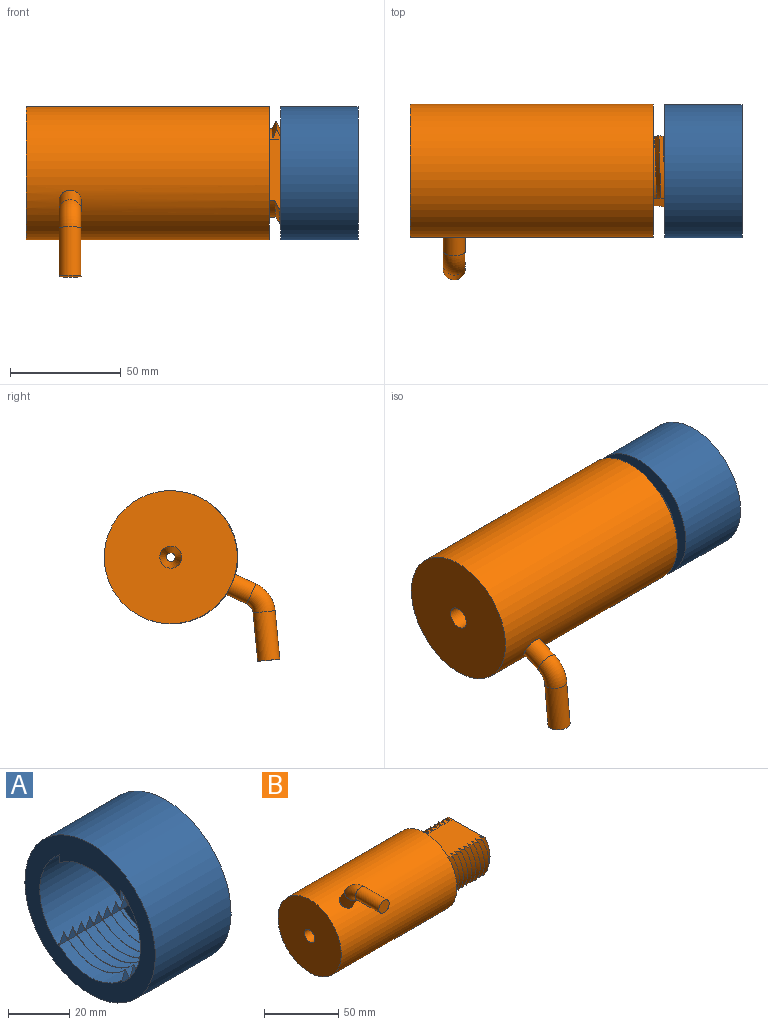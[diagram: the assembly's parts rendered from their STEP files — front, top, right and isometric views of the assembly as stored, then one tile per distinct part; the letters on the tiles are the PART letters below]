
ASSEMBLY  parts=2 mates=1
PART A: 97 faces, bbox 35x60.2x60.2 mm
  f0: cylinder r=20.1mm len=15.47mm, axis (-1,0,0), area 1.6mm2, adj f16,f25
  f1: cylinder r=20.1mm len=28.28mm, axis (-1,0,0), area 3.3mm2, adj f26,f35
  f2: cylinder r=20.1mm len=28.28mm, axis (-1,0,0), area 3.3mm2, adj f27,f36
  f3: cylinder r=20.1mm len=28.28mm, axis (-1,0,0), area 3.3mm2, adj f28,f37
  f4: cylinder r=20.1mm len=28.28mm, axis (-1,0,0), area 3.3mm2, adj f29,f38
  f5: cylinder r=20.1mm len=28.28mm, axis (-1,0,0), area 3.3mm2, adj f30,f39
  f6: cylinder r=20.1mm len=28.28mm, axis (-1,0,0), area 3.3mm2, adj f31,f40
  f7: cylinder r=20.1mm len=28.28mm, axis (-1,0,0), area 3.3mm2, adj f32,f41
  f8: cylinder r=20.1mm len=29.25mm, axis (-1,0,0), area 3.4mm2, adj f57,f61
  f9: cylinder r=20.1mm len=29.25mm, axis (-1,0,0), area 3.4mm2, adj f24,f51
  f10: cylinder r=20.1mm len=29.25mm, axis (-1,0,0), area 3.4mm2, adj f23,f50
  f11: cylinder r=20.1mm len=29.25mm, axis (-1,0,0), area 3.4mm2, adj f22,f49
  f12: cylinder r=20.1mm len=29.25mm, axis (-1,0,0), area 3.4mm2, adj f21,f48
  f13: cylinder r=20.1mm len=29.25mm, axis (-1,0,0), area 3.4mm2, adj f20,f47
  f14: cylinder r=20.1mm len=29.25mm, axis (-1,0,0), area 3.4mm2, adj f19,f46
  f15: cylinder r=20.1mm len=29.25mm, axis (-1,0,0), area 3.4mm2, adj f18,f45
  f16: plane 60.2x60.2mm, normal (-1,0,0), area 1237.9mm2, adj f0,f17,f25,f34,f43,f55,f56,f59
  f17: plane 4.26x3.45mm, normal (0,-1,0.02), area 8mm2, adj f16,f53,f56
  f18: plane 4.26x3.77mm, normal (0,-1,0.02), area 8.1mm2, adj f15,f56
  f19: plane 4.26x3.77mm, normal (0,-1,0.02), area 8.1mm2, adj f14,f56
  f20: plane 4.26x3.77mm, normal (0,-1,0.02), area 8.1mm2, adj f13,f56
  f21: plane 4.26x3.77mm, normal (0,-1,0.02), area 8.1mm2, adj f12,f56
  f22: plane 4.26x3.77mm, normal (0,-1,0.02), area 8.1mm2, adj f11,f56
  f23: plane 4.26x3.77mm, normal (0,-1,0.02), area 8.1mm2, adj f10,f56
  f24: plane 4.26x3.77mm, normal (0,-1,0.02), area 8.1mm2, adj f9,f56
  f25: plane 4.2x2.29mm, normal (0,-1,0), area 5.6mm2, adj f0,f16,f56
  f26: plane 4.2x3.77mm, normal (0,-1,0), area 8mm2, adj f1,f56
  f27: plane 4.2x3.77mm, normal (0,-1,0), area 8mm2, adj f2,f56
  f28: plane 4.2x3.77mm, normal (0,-1,0), area 8mm2, adj f3,f56
  f29: plane 4.2x3.77mm, normal (0,-1,0), area 8mm2, adj f4,f56
  f30: plane 4.2x3.77mm, normal (0,-1,0), area 8mm2, adj f5,f56
  f31: plane 4.2x3.77mm, normal (0,-1,0), area 8mm2, adj f6,f56
  f32: plane 4.2x3.77mm, normal (0,-1,0), area 8mm2, adj f7,f56
  f33: plane 4.2x3.77mm, normal (0,-1,0), area 8mm2, adj f52,f56
  f34: plane 3.18x1.47mm, normal (0,1,0), area 2.3mm2, adj f16,f59
  f35: plane 4.2x3.77mm, normal (0,1,0), area 8mm2, adj f1,f59
  f36: plane 4.2x3.77mm, normal (0,1,0), area 8mm2, adj f2,f59
  f37: plane 4.2x3.77mm, normal (0,1,0), area 8mm2, adj f3,f59
  f38: plane 4.2x3.77mm, normal (0,1,0), area 8mm2, adj f4,f59
  f39: plane 4.2x3.77mm, normal (0,1,0), area 8mm2, adj f5,f59
  f40: plane 4.2x3.77mm, normal (0,1,0), area 8mm2, adj f6,f59
  f41: plane 4.2x3.77mm, normal (0,1,0), area 8mm2, adj f7,f59
  f42: plane 4.2x3.77mm, normal (0,1,0), area 8mm2, adj f52,f59
  f43: plane 0.71x0.31mm, normal (0,1,0.02), area 0.1mm2, adj f16,f59
  f44: plane 4.26x3.77mm, normal (0,1,0.02), area 8.1mm2, adj f53,f59
  f45: plane 4.26x3.77mm, normal (0,1,0.02), area 8.1mm2, adj f15,f59
  f46: plane 4.26x3.77mm, normal (0,1,0.02), area 8.1mm2, adj f14,f59
  f47: plane 4.26x3.77mm, normal (0,1,0.02), area 8.1mm2, adj f13,f59
  f48: plane 4.26x3.77mm, normal (0,1,0.02), area 8.1mm2, adj f12,f59
  f49: plane 4.26x3.77mm, normal (0,1,0.02), area 8.1mm2, adj f11,f59
  f50: plane 4.26x3.77mm, normal (0,1,0.02), area 8.1mm2, adj f10,f59
  f51: plane 4.26x3.77mm, normal (0,1,0.02), area 8.1mm2, adj f9,f59
  f52: cylinder r=20.1mm len=28.28mm, axis (-1,0,0), area 3.3mm2, adj f33,f42
  f53: cylinder r=20.1mm len=29.25mm, axis (-1,0,0), area 3.4mm2, adj f17,f44
  f54: plane 60.2x60.2mm, normal (1,0,0), area 1241.2mm2, adj f55,f56,f57,f58,f59,f60,f61
  f55: cylinder r=30.1mm len=60.2mm, axis (-1,0,0), area 6619.3mm2, adj f16,f54
  f56: cylinder r=23.27mm len=36.53mm, axis (1,0,0), area 1469.9mm2, adj f16,f17,f18,f19,f20,f21,f22,f23
  f57: plane 4.26x3.32mm, normal (0,-1,0.02), area 7.9mm2, adj f8,f54,f56
  f58: plane 1.02x0.48mm, normal (0,-1,0), area 0.2mm2, adj f54,f56
  f59: cylinder r=23.27mm len=36.53mm, axis (1,0,0), area 1469.9mm2, adj f16,f34,f35,f36,f37,f38,f39,f40
  f60: plane 3.07x1.3mm, normal (0,1,0), area 2mm2, adj f54,f59
  f61: plane 4.26x2.46mm, normal (0,1,0.02), area 6.1mm2, adj f8,f54,f59
  f62: plane 0.26x0.23mm, normal (0,-1,-0.02), area 0mm2, adj f59
  f63: plane 0.26x0.23mm, normal (0,1,-0.02), area 0mm2, adj f56
  f64: plane 0.26x0.23mm, normal (0,-1,-0.02), area 0mm2, adj f59
  f65: plane 0.26x0.23mm, normal (0,1,-0.02), area 0mm2, adj f56
  f66: plane 0.26x0.23mm, normal (0,-1,-0.02), area 0mm2, adj f59
  f67: plane 0.26x0.23mm, normal (0,1,-0.02), area 0mm2, adj f56
  f68: plane 0.26x0.23mm, normal (0,-1,-0.02), area 0mm2, adj f59
  f69: plane 0.26x0.23mm, normal (0,1,-0.02), area 0mm2, adj f56
  f70: plane 0.26x0.23mm, normal (0,-1,-0.02), area 0mm2, adj f59
  f71: plane 0.26x0.23mm, normal (0,1,-0.02), area 0mm2, adj f56
  f72: plane 0.26x0.23mm, normal (0,-1,-0.02), area 0mm2, adj f59
  f73: plane 0.26x0.23mm, normal (0,1,-0.02), area 0mm2, adj f56
  f74: plane 0.26x0.23mm, normal (0,-1,-0.02), area 0mm2, adj f59
  f75: plane 0.26x0.23mm, normal (0,1,-0.02), area 0mm2, adj f56
  f76: plane 0.26x0.23mm, normal (0,-1,-0.02), area 0mm2, adj f59
  f77: plane 0.26x0.23mm, normal (0,1,-0.02), area 0mm2, adj f56
  f78: plane 0.26x0.23mm, normal (0,-1,-0.02), area 0mm2, adj f59
  f79: plane 0.25x0.23mm, normal (0,-1,0), area 0mm2, adj f59
  f80: plane 0.25x0.23mm, normal (0,1,0), area 0mm2, adj f56
  f81: plane 0.25x0.23mm, normal (0,-1,0), area 0mm2, adj f59
  f82: plane 0.25x0.23mm, normal (0,1,0), area 0mm2, adj f56
  f83: plane 0.25x0.23mm, normal (0,-1,0), area 0mm2, adj f59
  f84: plane 0.25x0.23mm, normal (0,1,0), area 0mm2, adj f56
  f85: plane 0.25x0.23mm, normal (0,-1,0), area 0mm2, adj f59
  f86: plane 0.25x0.23mm, normal (0,1,0), area 0mm2, adj f56
  f87: plane 0.25x0.23mm, normal (0,-1,0), area 0mm2, adj f59
  f88: plane 0.25x0.23mm, normal (0,1,0), area 0mm2, adj f56
  f89: plane 0.25x0.23mm, normal (0,-1,0), area 0mm2, adj f59
  f90: plane 0.25x0.23mm, normal (0,1,0), area 0mm2, adj f56
  f91: plane 0.25x0.23mm, normal (0,-1,0), area 0mm2, adj f59
  f92: plane 0.25x0.23mm, normal (0,1,0), area 0mm2, adj f56
  f93: plane 0.25x0.23mm, normal (0,-1,0), area 0mm2, adj f59
  f94: plane 0.25x0.23mm, normal (0,1,0), area 0mm2, adj f56
  f95: plane 0.25x0.23mm, normal (0,-1,0), area 0mm2, adj f59
  f96: plane 0.25x0.23mm, normal (0,1,0), area 0mm2, adj f56
PART B: 98 faces, bbox 152.8x81.6x76.8 mm
  f0: bspline ~46.55x26.87mm, area 117.4mm2, adj f20,f50,f66,f80
  f1: bspline ~46.55x26.87mm, area 117.4mm2, adj f21,f51,f67,f81
  f2: bspline ~46.55x26.87mm, area 117.4mm2, adj f22,f52,f68,f82
  f3: bspline ~46.55x26.87mm, area 117.4mm2, adj f23,f53,f69,f83
  f4: bspline ~46.55x26.87mm, area 117.4mm2, adj f24,f54,f70,f84
  f5: bspline ~46.55x26.87mm, area 117.4mm2, adj f25,f55,f71,f85
  f6: bspline ~46.55x26.87mm, area 117.4mm2, adj f26,f56,f72,f86
  f7: bspline ~46.55x26.87mm, area 117.4mm2, adj f27,f57,f73,f87
  f8: bspline ~46.55x26.87mm, area 117.4mm2, adj f28,f58,f74,f88
  f9: bspline ~46.55x26.87mm, area 117.4mm2, adj f29,f59,f78,f91
  f10: bspline ~46.55x26.87mm, area 122.7mm2, adj f30,f49,f77,f92
  f11: bspline ~46.55x26.87mm, area 122.7mm2, adj f31,f48,f77,f92
  f12: bspline ~46.55x26.87mm, area 122.7mm2, adj f32,f47,f77,f92
  f13: bspline ~46.55x26.87mm, area 122.7mm2, adj f33,f46,f77,f92
  f14: bspline ~46.55x26.87mm, area 122.7mm2, adj f34,f45,f77,f92
  f15: bspline ~46.55x26.87mm, area 122.7mm2, adj f35,f44,f77,f92
  f16: bspline ~46.55x26.87mm, area 122.7mm2, adj f36,f43,f77,f92
  f17: bspline ~46.55x26.87mm, area 122.7mm2, adj f37,f42,f77,f92
  f18: bspline ~46.55x26.87mm, area 122.7mm2, adj f38,f41,f77,f92
  f19: bspline ~46.55x26.87mm, area 58mm2, adj f39,f40,f77,f92
  f20: bspline ~46.55x26.87mm, area 117.4mm2, adj f0,f51,f66,f80
  f21: bspline ~46.55x26.87mm, area 117.4mm2, adj f1,f52,f67,f81
  f22: bspline ~46.55x26.87mm, area 117.4mm2, adj f2,f53,f68,f82
  f23: bspline ~46.55x26.87mm, area 117.4mm2, adj f3,f54,f69,f83
  f24: bspline ~46.55x26.87mm, area 117.4mm2, adj f4,f55,f70,f84
  f25: bspline ~46.55x26.87mm, area 117.4mm2, adj f5,f56,f71,f85
  f26: bspline ~46.55x26.87mm, area 117.4mm2, adj f6,f57,f72,f86
  f27: bspline ~46.55x26.87mm, area 117.4mm2, adj f7,f58,f73,f87
  f28: bspline ~46.55x26.87mm, area 117.4mm2, adj f8,f59,f74,f88
  f29: bspline ~46.55x26.87mm, area 62.4mm2, adj f9,f39,f78,f91
  f30: bspline ~46.55x26.87mm, area 122.7mm2, adj f10,f48,f77,f92
  f31: bspline ~46.55x26.87mm, area 122.7mm2, adj f11,f47,f77,f92
  f32: bspline ~46.55x26.87mm, area 122.7mm2, adj f12,f46,f77,f92
  f33: bspline ~46.55x26.87mm, area 122.7mm2, adj f13,f45,f77,f92
  f34: bspline ~46.55x26.87mm, area 122.7mm2, adj f14,f44,f77,f92
  f35: bspline ~46.55x26.87mm, area 122.7mm2, adj f15,f43,f77,f92
  f36: bspline ~46.55x26.87mm, area 122.7mm2, adj f16,f42,f77,f92
  f37: bspline ~46.55x26.87mm, area 122.7mm2, adj f17,f41,f77,f92
  f38: bspline ~46.55x26.87mm, area 122.7mm2, adj f18,f40,f77,f92
  f39: plane 43.95x30.12mm, normal (1,0,0), area 1126.5mm2, adj f19,f29,f61,f77,f78,f91,f92
  f40: cylinder r=20mm len=29.24mm, axis (-1,0,0), area 7.2mm2, adj f19,f38,f77,f92
  f41: cylinder r=20mm len=29.24mm, axis (-1,0,0), area 7.2mm2, adj f18,f37,f77,f92
  f42: cylinder r=20mm len=29.24mm, axis (-1,0,0), area 7.2mm2, adj f17,f36,f77,f92
  f43: cylinder r=20mm len=29.24mm, axis (-1,0,0), area 7.2mm2, adj f16,f35,f77,f92
  f44: cylinder r=20mm len=29.24mm, axis (-1,0,0), area 7.2mm2, adj f15,f34,f77,f92
  f45: cylinder r=20mm len=29.24mm, axis (-1,0,0), area 7.2mm2, adj f14,f33,f77,f92
  f46: cylinder r=20mm len=29.24mm, axis (-1,0,0), area 7.2mm2, adj f13,f32,f77,f92
  f47: cylinder r=20mm len=29.24mm, axis (-1,0,0), area 7.2mm2, adj f12,f31,f77,f92
  f48: cylinder r=20mm len=29.24mm, axis (-1,0,0), area 7.2mm2, adj f11,f30,f77,f92
  f49: cylinder r=20mm len=29.24mm, axis (-1,0,0), area 101.7mm2, adj f10,f60,f77,f92
  f50: cylinder r=20mm len=28.28mm, axis (-1,0,0), area 34.6mm2, adj f0,f60,f77,f92
  f51: cylinder r=20mm len=28.28mm, axis (-1,0,0), area 6.9mm2, adj f1,f20,f77,f92
  f52: cylinder r=20mm len=28.28mm, axis (-1,0,0), area 6.9mm2, adj f2,f21,f77,f92
  f53: cylinder r=20mm len=28.28mm, axis (-1,0,0), area 6.9mm2, adj f3,f22,f77,f92
  f54: cylinder r=20mm len=28.28mm, axis (-1,0,0), area 6.9mm2, adj f4,f23,f77,f92
  f55: cylinder r=20mm len=28.28mm, axis (-1,0,0), area 6.9mm2, adj f5,f24,f77,f92
  f56: cylinder r=20mm len=28.28mm, axis (-1,0,0), area 6.9mm2, adj f6,f25,f77,f92
  f57: cylinder r=20mm len=28.28mm, axis (-1,0,0), area 6.9mm2, adj f7,f26,f77,f92
  f58: cylinder r=20mm len=28.28mm, axis (-1,0,0), area 6.9mm2, adj f8,f27,f77,f92
  f59: cylinder r=20mm len=28.28mm, axis (-1,0,0), area 6.9mm2, adj f9,f28,f77,f92
  f60: plane 60.2x60.2mm, normal (1,0,0), area 1351.2mm2, adj f49,f50,f62,f75,f76,f77,f89,f90
  f61: cylinder r=2mm len=15mm, axis (-1,0,0), area 188.5mm2, adj f39,f65
  f62: cylinder r=30.1mm len=110mm, axis (-1,0,0), area 20725mm2, adj f60,f63,f94
  f63: plane 60.2x60.2mm, normal (-1,0,0), area 2767.8mm2, adj f62,f64
  f64: cylinder r=5mm len=120.3mm, axis (-1,0,0), area 3779.4mm2, adj f63,f65
  f65: cone r=2mm half-angle=11.5deg, axis (-1,0,0), area 329.9mm2, adj f61,f64
  f66: plane 4.58x4.01mm, normal (0,0,1), area 8.4mm2, adj f0,f20,f77
  f67: plane 4.58x4.01mm, normal (0,0,1), area 8.4mm2, adj f1,f21,f77
  f68: plane 4.58x4.01mm, normal (0,0,1), area 8.4mm2, adj f2,f22,f77
  f69: plane 4.58x4.01mm, normal (0,0,1), area 8.4mm2, adj f3,f23,f77
  f70: plane 4.58x4.01mm, normal (0,0,1), area 8.4mm2, adj f4,f24,f77
  f71: plane 4.58x4.01mm, normal (0,0,1), area 8.4mm2, adj f5,f25,f77
  f72: plane 4.58x4.01mm, normal (0,0,1), area 8.4mm2, adj f6,f26,f77
  f73: plane 4.58x4.01mm, normal (0,0,1), area 8.4mm2, adj f7,f27,f77
  f74: plane 4.58x4.01mm, normal (0,0,1), area 8.4mm2, adj f8,f28,f77
  f75: plane 10x4.34mm, normal (0,0,1), area 43.4mm2, adj f60,f76,f77,f79
  f76: cylinder r=23.27mm len=36.53mm, axis (1,0,0), area 420.1mm2, adj f60,f75,f77,f79
  f77: plane 50.24x32.43mm, normal (0,0.02,1), area 1512.4mm2, adj f10,f11,f12,f13,f14,f15,f16,f17
  f78: plane 4.58x2.64mm, normal (0,0,1), area 6.2mm2, adj f9,f29,f39,f77
  f79: plane 36.53x9.13mm, normal (1,0,0), area 226.7mm2, adj f75,f76,f77
  f80: plane 4.58x4.01mm, normal (0,0,-1), area 8.4mm2, adj f0,f20,f92
  f81: plane 4.58x4.01mm, normal (0,0,-1), area 8.4mm2, adj f1,f21,f92
  f82: plane 4.58x4.01mm, normal (0,0,-1), area 8.4mm2, adj f2,f22,f92
  f83: plane 4.58x4.01mm, normal (0,0,-1), area 8.4mm2, adj f3,f23,f92
  f84: plane 4.58x4.01mm, normal (0,0,-1), area 8.4mm2, adj f4,f24,f92
  f85: plane 4.58x4.01mm, normal (0,0,-1), area 8.4mm2, adj f5,f25,f92
  f86: plane 4.58x4.01mm, normal (0,0,-1), area 8.4mm2, adj f6,f26,f92
  f87: plane 4.58x4.01mm, normal (0,0,-1), area 8.4mm2, adj f7,f27,f92
  f88: plane 4.58x4.01mm, normal (0,0,-1), area 8.4mm2, adj f8,f28,f92
  f89: plane 10x4.34mm, normal (0,0,-1), area 43.4mm2, adj f60,f90,f92,f93
  f90: cylinder r=23.27mm len=36.53mm, axis (1,0,0), area 420.1mm2, adj f60,f89,f92,f93
  f91: plane 4.57x3.62mm, normal (0,0,-1), area 8.2mm2, adj f9,f29,f39,f92
  f92: plane 50.24x32.43mm, normal (0,0.02,-1), area 1510.3mm2, adj f10,f11,f12,f13,f14,f15,f16,f17
  f93: plane 36.53x9.13mm, normal (1,0,0), area 226.7mm2, adj f89,f90,f92
  f94: cylinder r=5mm len=13.94mm, axis (0,0.5,-0.87), area 324.2mm2, adj f62,f97
  f95: plane 10x10mm, normal (0,-1,0), area 78.5mm2, adj f96
  f96: cylinder r=5mm len=22.03mm, axis (0,1,0), area 692mm2, adj f95,f97
  f97: torus R=10mm, axis (-1,0,0), area 329mm2, adj f94,f96
PLACE A at identity fixed
PLACE B rot(axis=(1,0,0),84.5deg) t=(-0.18,0.23,0.08)mm
MATE cylindrical B.f39 <-> A.f0  axis (1,0,0) through (149.82,0,0)mm
